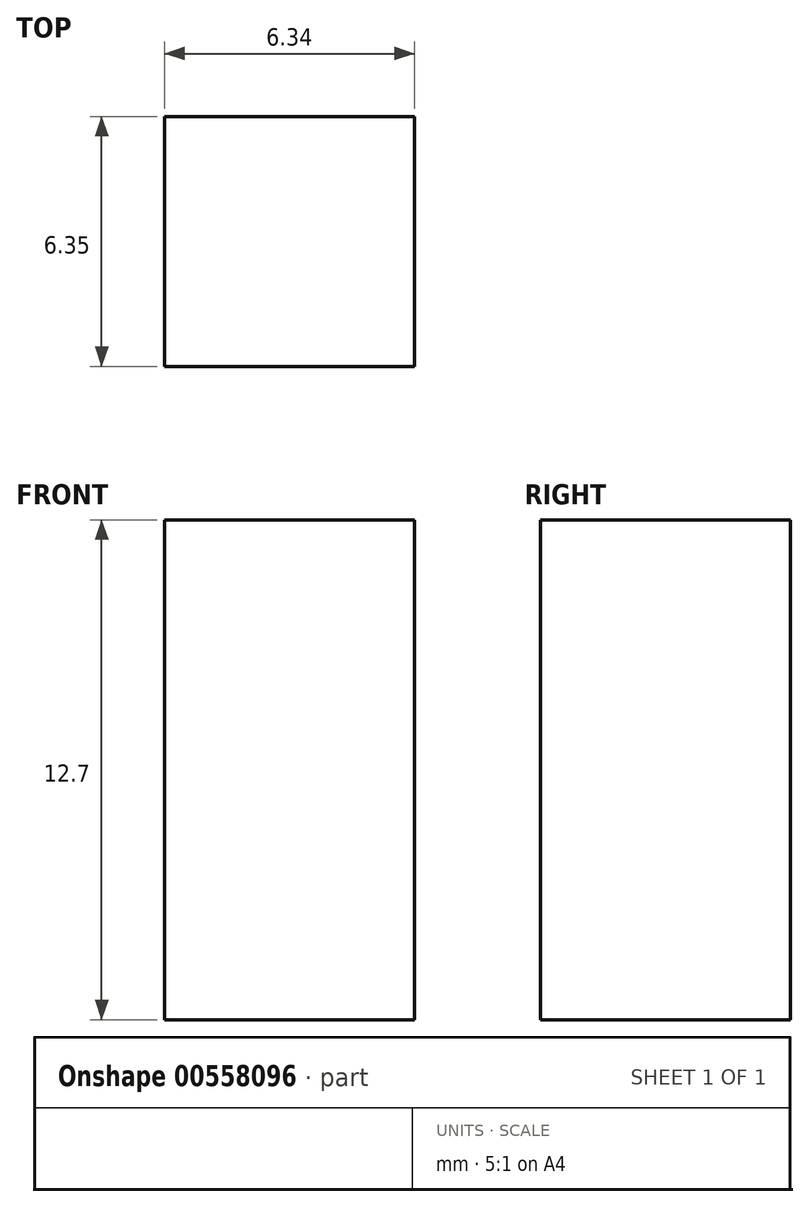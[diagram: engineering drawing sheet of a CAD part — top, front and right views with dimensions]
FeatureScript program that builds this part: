
annotation { "Feature Type Name" : "Feature", "Feature Type Description" : "" }
export const myFeature = defineFeature(function(context is Context, id is Id, definition is map)
    precondition{}
    {
        {
            var Q0;
            Q0=qCreatedBy(makeId("Front.planeOp"),FACE);
            var sketch = newSketch(context, id + "F0", { "sketchPlane" : qUnion([Q0])});
            skLineSegment(sketch, "E0.bottom", {"start": v(3.18, -6.35) * mm, "end": v(-3.18, -6.35) * mm});
            skLineSegment(sketch, "E0.top", {"start": v(3.18, 6.35) * mm, "end": v(-3.17, 6.35) * mm});
            skLineSegment(sketch, "E0.left", {"start": v(3.18, -6.35) * mm, "end": v(3.18, 6.35) * mm});
            skLineSegment(sketch, "E0.right", {"start": v(-3.18, -6.35) * mm, "end": v(-3.17, 6.35) * mm});
            skPoint(sketch, "E0.middle", {"position": v(0, 0) * mm});
            skSolve(sketch);
        }
        {
            var Q0;
            Q0 = qSketchRegion(id + "F0", true);
            extrude(context, id + "F1", {"entities" : qUnion([Q0]), "depth" : 6.35 * mm, "offsetDistance" : 25.4 * mm});
        }
    });
